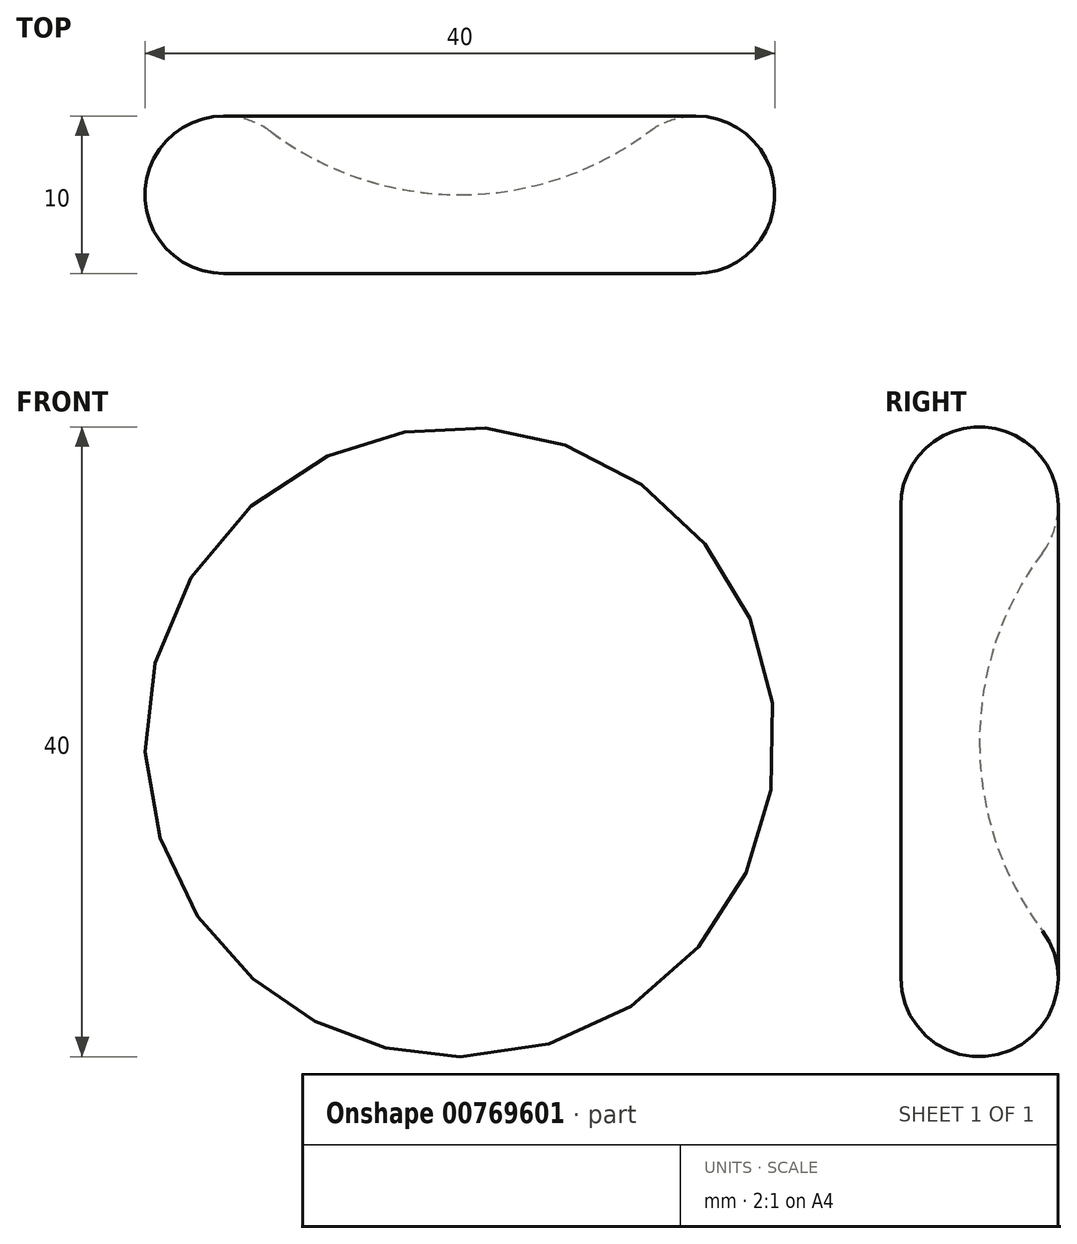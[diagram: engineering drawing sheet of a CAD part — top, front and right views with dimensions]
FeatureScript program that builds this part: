
annotation { "Feature Type Name" : "Feature", "Feature Type Description" : "" }
export const myFeature = defineFeature(function(context is Context, id is Id, definition is map)
    precondition{}
    {
        {
            var Q0;
            Q0=qCreatedBy(makeId("Top.planeOp"),FACE);
            var sketch = newSketch(context, id + "F0", { "sketchPlane" : qUnion([Q0])});
            skArc(sketch, "E0", {"start": v(-12, 9) * mm, "mid": v(-6.32, 6.03) * mm, "end": v(0, 5) * mm});
            skArc(sketch, "E1", {"start": v(-12, 9) * mm, "mid": v(-19.74, 6.58) * mm, "end": v(-15, 0) * mm});
            skLineSegment(sketch, "E2", {"start": v(-15, 0) * mm, "end": v(0, 0) * mm});
            skLineSegment(sketch, "E3", {"start": v(0, 0) * mm, "end": v(0, 5) * mm});
            skPoint(sketch, "E4.orphan", {"position": v(-14.77, 0) * mm});
            skSolve(sketch);
        }
        {
            var Q0;
            Q0=makeQuery(id+"F0.imprint","IMPRINT",FACE,{"disambiguationData":[TD([[makeQuery(id+"F0.imprint","IMPRINT",EDGE,{"derivedFrom":sQuery(id+"F0.wireOp",EDGE,"E0")}),-1.0]])]});
            var Q1;
            Q1=sQuery(id+"F0.wireOp",EDGE,"E3");
            revolve(context, id + "F1", {"surfaceOperationType" : NewSurfaceOperationType.NEW, "entities" : qUnion([Q0]), "axis" : qUnion([Q1]), "revolveType" : RevolveType.FULL});
        }
    });
